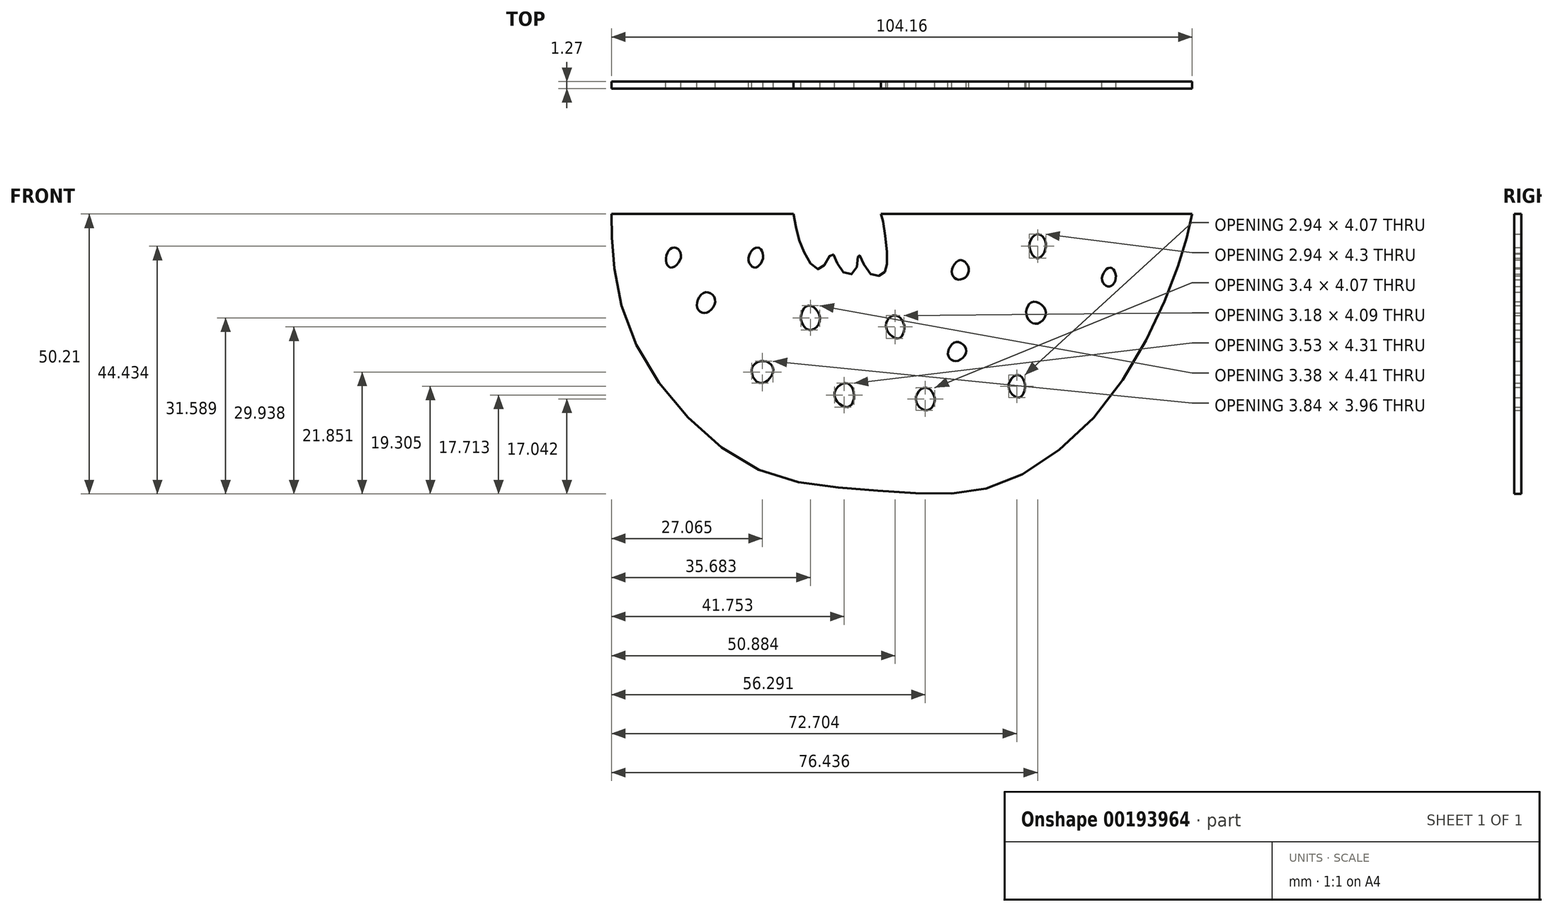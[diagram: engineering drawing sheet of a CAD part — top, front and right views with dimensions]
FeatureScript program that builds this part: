
annotation { "Feature Type Name" : "Feature", "Feature Type Description" : "" }
export const myFeature = defineFeature(function(context is Context, id is Id, definition is map)
    precondition{}
    {
        {
            var Q0;
            Q0=qCreatedBy(makeId("Front.planeOp"),FACE);
            var sketch = newSketch(context, id + "F0", { "sketchPlane" : qUnion([Q0])});
            skFitSpline(sketch, "E0", {"points": [v(-13.56, 24.78) * mm, v(-11.48, 17.56) * mm, v(-8.62, 14.96) * mm, v(-6.67, 17.7) * mm, v(-4.98, 14.7) * mm, v(-2.5, 14.44) * mm, v(-1.86, 17.56) * mm, v(0.1, 14.18) * mm, v(2.56, 14.05) * mm, v(3.21, 17.82) * mm, v(2.17, 24.78) * mm, v(2.09, 24.78) * mm], "startDerivative": vector(10.52, -55) * mm, "endDerivative": vector(-5.65, -3.15) * mm});
            skLineSegment(sketch, "E1", {"start": v(-41.96, 24.78) * mm, "end": v(-41.96, 18.66) * mm});
            skLineSegment(sketch, "E2", {"start": v(-41.96, 18.66) * mm, "end": v(-39.7, 8.25) * mm});
            skLineSegment(sketch, "E3", {"start": v(-39.7, 8.25) * mm, "end": v(-30.3, -7.14) * mm});
            skLineSegment(sketch, "E4", {"start": v(-30.3, -7.14) * mm, "end": v(-15.36, -18.24) * mm});
            skLineSegment(sketch, "E5", {"start": v(-15.36, -18.24) * mm, "end": v(-2.8, -19.6) * mm});
            skLineSegment(sketch, "E6", {"start": v(-2.8, -19.6) * mm, "end": v(5.34, -19.6) * mm});
            skLineSegment(sketch, "E7", {"start": v(5.34, -19.6) * mm, "end": v(11.58, -19.6) * mm});
            skLineSegment(sketch, "E8", {"start": v(11.58, -19.6) * mm, "end": v(21.32, -18.24) * mm});
            skLineSegment(sketch, "E9", {"start": v(21.32, -18.24) * mm, "end": v(36.37, -7.71) * mm});
            skLineSegment(sketch, "E10", {"start": v(36.37, -7.71) * mm, "end": v(47.46, 7.64) * mm});
            skLineSegment(sketch, "E11", {"start": v(47.46, 7.64) * mm, "end": v(51.06, 19.23) * mm});
            skLineSegment(sketch, "E12", {"start": v(51.06, 19.23) * mm, "end": v(52.45, 24.78) * mm});
            skFitSpline(sketch, "E13", {"points": [v(-34.94, 18.78) * mm, v(-36.41, 16.97) * mm, v(-35.5, 15.16) * mm, v(-33.7, 17.2) * mm, v(-34.94, 18.78) * mm]});
            skFitSpline(sketch, "E14", {"points": [v(-20, 18.78) * mm, v(-21.59, 16.85) * mm, v(-20.45, 15.16) * mm, v(-18.98, 17.08) * mm, v(-20, 18.78) * mm]});
            skFitSpline(sketch, "E15", {"points": [v(-29.28, 10.74) * mm, v(-30.87, 8.36) * mm, v(-29.4, 7) * mm, v(-27.59, 9.27) * mm, v(-29.28, 10.74) * mm]});
            skFitSpline(sketch, "E16", {"points": [v(-18.87, -1.6) * mm, v(-21.02, -3.07) * mm, v(-19.44, -5.56) * mm, v(-17.17, -3.3) * mm, v(-18.87, -1.6) * mm]});
            skFitSpline(sketch, "E17", {"points": [v(-10.83, 8.36) * mm, v(-12.2, 5.99) * mm, v(-10.5, 3.95) * mm, v(-8.8, 6.1) * mm, v(-10.83, 8.36) * mm]});
            skFitSpline(sketch, "E18", {"points": [v(-4.27, -5.56) * mm, v(-6.2, -7.71) * mm, v(-3.81, -9.86) * mm, v(-2.68, -7.37) * mm, v(-4.27, -5.56) * mm]});
            skFitSpline(sketch, "E19", {"points": [v(4.34, 6.55) * mm, v(3.1, 4.4) * mm, v(5.34, 2.48) * mm, v(6.26, 5.08) * mm, v(4.34, 6.55) * mm]});
            skFitSpline(sketch, "E20", {"points": [v(10.22, -6.35) * mm, v(8.41, -8.4) * mm, v(10.22, -10.43) * mm, v(11.8, -8.73) * mm, v(10.22, -6.35) * mm]});
            skFitSpline(sketch, "E21", {"points": [v(15.66, 1.8) * mm, v(14.18, -0.35) * mm, v(15.66, -1.6) * mm, v(17.47, 0.33) * mm, v(15.66, 1.8) * mm]});
            skFitSpline(sketch, "E22", {"points": [v(16.45, 16.51) * mm, v(14.86, 14.36) * mm, v(16.22, 13) * mm, v(17.92, 14.59) * mm, v(16.45, 16.51) * mm]});
            skFitSpline(sketch, "E23", {"points": [v(30.37, 21.15) * mm, v(28.79, 19.23) * mm, v(30.26, 16.85) * mm, v(31.73, 19.23) * mm, v(30.37, 21.15) * mm]});
            skFitSpline(sketch, "E24", {"points": [v(29.58, 9.04) * mm, v(28.22, 7) * mm, v(29.92, 5.08) * mm, v(31.73, 7.12) * mm, v(29.58, 9.04) * mm]});
            skFitSpline(sketch, "E25", {"points": [v(26.75, -4.09) * mm, v(25.05, -6.13) * mm, v(26.86, -8.16) * mm, v(28, -6.13) * mm, v(26.75, -4.09) * mm]});
            skFitSpline(sketch, "E26", {"points": [v(43.28, 15.16) * mm, v(41.8, 13.23) * mm, v(43.05, 11.76) * mm, v(44.3, 13.34) * mm, v(43.28, 15.16) * mm]});
            skFitSpline(sketch, "E27", {"points": [v(-46.18, 24.78) * mm, v(-46.02, 18.66) * mm, v(-43.49, 5.42) * mm, v(-33.37, -10.76) * mm, v(-17.87, -21.89) * mm, v(-1.85, -24.58) * mm, v(12.3, -25.43) * mm, v(24.6, -23.28) * mm, v(40.45, -11.6) * mm, v(51.75, 6.26) * mm, v(56.47, 18.66) * mm, v(57.98, 24.78) * mm], "startDerivative": vector(0.19, -92.76) * mm, "endDerivative": vector(20.57, 93.54) * mm});
            skLineSegment(sketch, "E28", {"start": v(-13.56, 24.78) * mm, "end": v(-41.96, 24.78) * mm});
            skLineSegment(sketch, "E29", {"start": v(-46.18, 24.78) * mm, "end": v(-41.96, 24.78) * mm});
            skLineSegment(sketch, "E30", {"start": v(2.17, 24.78) * mm, "end": v(52.45, 24.78) * mm});
            skLineSegment(sketch, "E31", {"start": v(52.45, 24.78) * mm, "end": v(57.98, 24.78) * mm});
            skSolve(sketch);
        }
        {
            var Q0;
            Q0=makeQuery(id+"F0.imprint","IMPRINT",FACE,{"disambiguationData":[TD([[makeQuery(id+"F0.imprint","IMPRINT",EDGE,{"derivedFrom":sQuery(id+"F0.wireOp",EDGE,"E1")}),1.0]])]});
            var Q1;
            Q1=makeQuery(id+"F0.imprint","IMPRINT",FACE,{"disambiguationData":[TD([[makeQuery(id+"F0.imprint","IMPRINT",EDGE,{"derivedFrom":sQuery(id+"F0.wireOp",EDGE,"E1")}),-1.0]])]});
            extrude(context, id + "F1", {"entities" : qUnion([Q0, Q1]), "depth" : 1.27 * mm});
        }
    });
